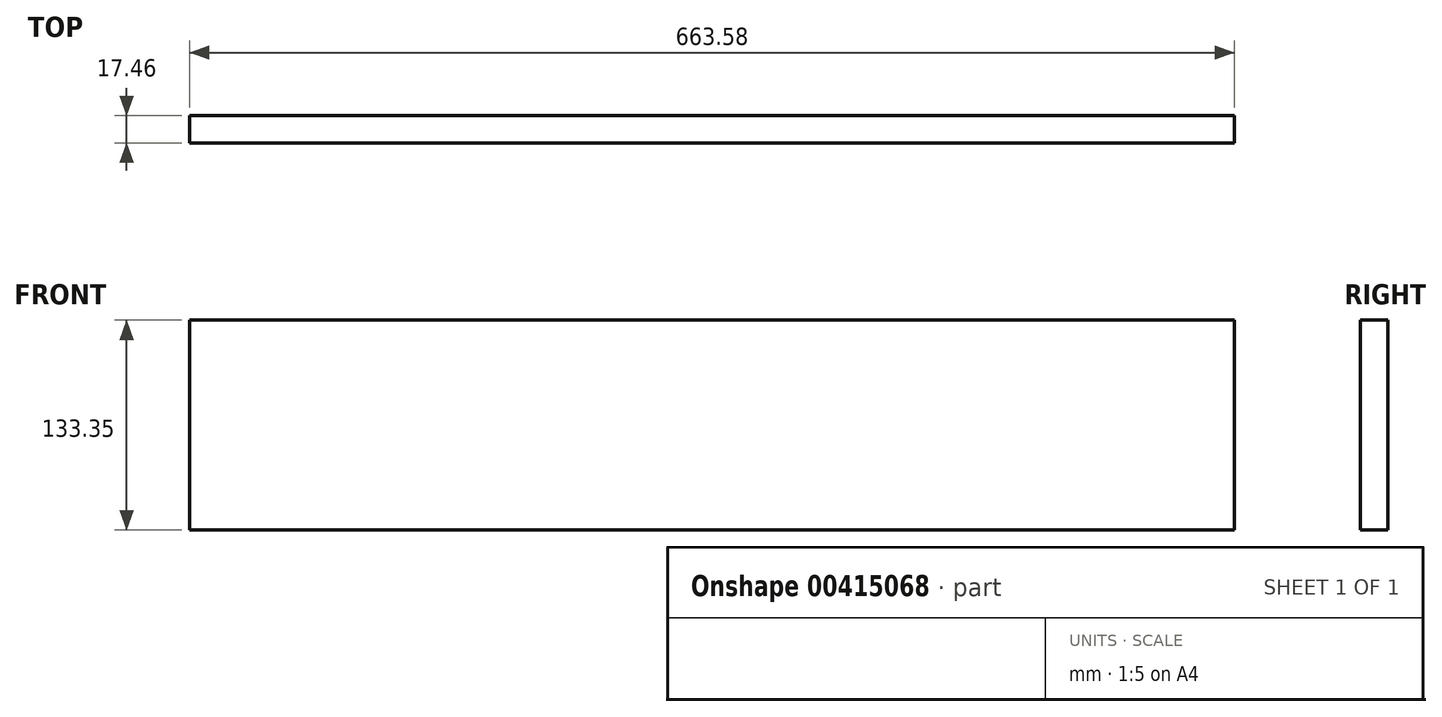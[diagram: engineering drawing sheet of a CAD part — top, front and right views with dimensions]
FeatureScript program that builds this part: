
annotation { "Feature Type Name" : "Feature", "Feature Type Description" : "" }
export const myFeature = defineFeature(function(context is Context, id is Id, definition is map)
    precondition{}
    {
        {
            var Q0;
            Q0=qCreatedBy(makeId("Front.planeOp"),FACE);
            var sketch = newSketch(context, id + "F0", { "sketchPlane" : qUnion([Q0])});
            skLineSegment(sketch, "E0.bottom", {"start": v(0, 0) * mm, "end": v(663.58, 0) * mm});
            skLineSegment(sketch, "E0.top", {"start": v(0, 133.35) * mm, "end": v(663.58, 133.35) * mm});
            skLineSegment(sketch, "E0.left", {"start": v(0, 0) * mm, "end": v(0, 133.35) * mm});
            skLineSegment(sketch, "E0.right", {"start": v(663.58, 0) * mm, "end": v(663.58, 133.35) * mm});
            skSolve(sketch);
        }
        {
            var Q0;
            Q0=makeQuery(id+"F0.imprint","IMPRINT",FACE,{"disambiguationData":[TD([[makeQuery(id+"F0.imprint","IMPRINT",EDGE,{"derivedFrom":sQuery(id+"F0.wireOp",EDGE,"E0.bottom")}),1.0]])]});
            extrude(context, id + "F1", {"entities" : qUnion([Q0]), "depth" : 17.46 * mm, "offsetDistance" : 25.4 * mm});
        }
    });
